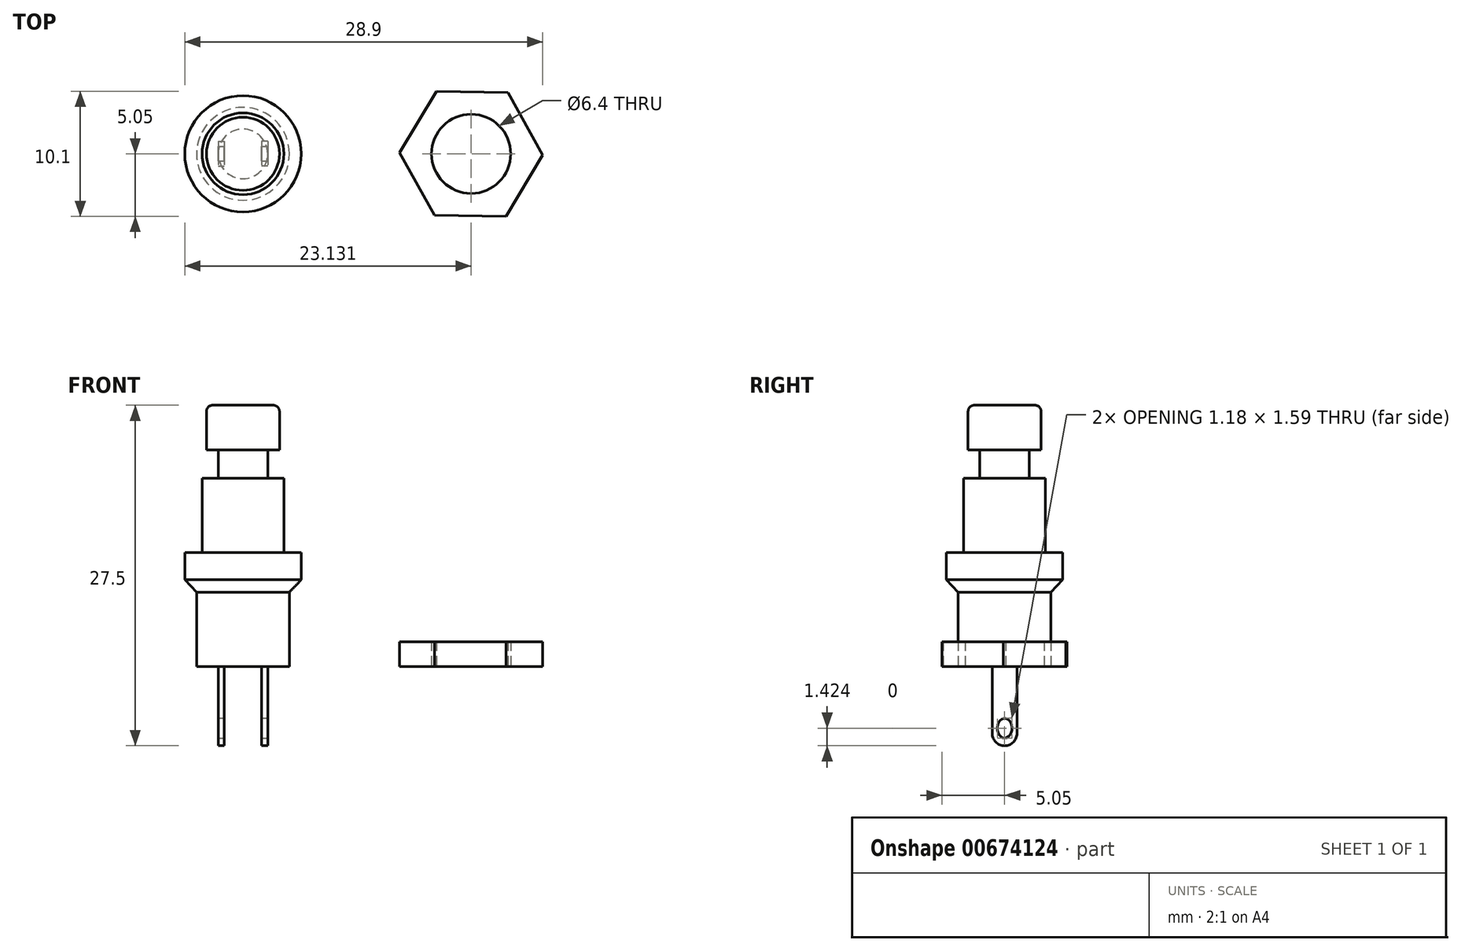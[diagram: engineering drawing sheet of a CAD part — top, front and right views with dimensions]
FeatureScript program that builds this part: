
annotation { "Feature Type Name" : "Feature", "Feature Type Description" : "" }
export const myFeature = defineFeature(function(context is Context, id is Id, definition is map)
    precondition{}
    {
        {
            var Q0;
            Q0=qCreatedBy(makeId("Top.planeOp"),FACE);
            var sketch = newSketch(context, id + "F0", { "sketchPlane" : qUnion([Q0])});
            skCircle(sketch, "E0", {"center": v(0, 0) * mm, "radius": 3.75 * mm});
            skLineSegment(sketch, "E1.bottom", {"start": v(-2, 1) * mm, "end": v(-1.5, 1) * mm});
            skLineSegment(sketch, "E1.top", {"start": v(-2, -1) * mm, "end": v(-1.5, -1) * mm});
            skLineSegment(sketch, "E1.left", {"start": v(-2, 1) * mm, "end": v(-2, -1) * mm});
            skLineSegment(sketch, "E1.right", {"start": v(-1.5, 1) * mm, "end": v(-1.5, -1) * mm});
            skLineSegment(sketch, "E2.MirrorCS", {"start": v(1.5, 1) * mm, "end": v(1.5, -1) * mm});
            skLineSegment(sketch, "E3.MirrorCS", {"start": v(2, 1) * mm, "end": v(1.5, 1) * mm});
            skLineSegment(sketch, "E4.MirrorCS", {"start": v(2, 1) * mm, "end": v(2, -1) * mm});
            skLineSegment(sketch, "E5.MirrorCS", {"start": v(2, -1) * mm, "end": v(1.5, -1) * mm});
            skCircle(sketch, "E6", {"center": v(18.43, 0) * mm, "radius": 3.2 * mm});
            skCircle(sketch, "E7.cCircle", {"center": v(18.43, 0) * mm, "radius": 5 * mm, "construction": true});
            skLineSegment(sketch, "E7.0", {"start": v(21.4, 4.95) * mm, "end": v(24.2, -0.1) * mm});
            skLineSegment(sketch, "E7.1", {"start": v(24.2, -0.1) * mm, "end": v(21.24, -5.05) * mm});
            skLineSegment(sketch, "E7.2", {"start": v(21.24, -5.05) * mm, "end": v(15.46, -4.95) * mm});
            skLineSegment(sketch, "E7.3", {"start": v(15.46, -4.95) * mm, "end": v(12.66, 0.1) * mm});
            skLineSegment(sketch, "E7.4", {"start": v(12.66, 0.1) * mm, "end": v(15.63, 5.05) * mm});
            skLineSegment(sketch, "E7.5", {"start": v(15.63, 5.05) * mm, "end": v(21.4, 4.95) * mm});
            skPoint(sketch, "E7.0.midPoint", {"position": v(22.8, 2.43) * mm});
            skSolve(sketch);
        }
        {
            var Q0;
            Q0=makeQuery(id+"F0.imprint","IMPRINT",FACE,{"disambiguationData":[TD([[makeQuery(id+"F0.imprint","IMPRINT",EDGE,{"derivedFrom":sQuery(id+"F0.wireOp",EDGE,"E0")}),1.0]])]});
            var Q1;
            Q1=makeQuery(id+"F0.imprint","IMPRINT",FACE,{"disambiguationData":[TD([[makeQuery(id+"F0.imprint","IMPRINT",EDGE,{"derivedFrom":sQuery(id+"F0.wireOp",EDGE,"E1.bottom")}),-1.0]])]});
            var Q2;
            Q2=makeQuery(id+"F0.imprint","IMPRINT",FACE,{"disambiguationData":[TD([[makeQuery(id+"F0.imprint","IMPRINT",EDGE,{"derivedFrom":sQuery(id+"F0.wireOp",EDGE,"E2.MirrorCS")}),1.0]])]});
            extrude(context, id + "F1", {"entities" : qUnion([Q0, Q1, Q2]), "depth" : 6 * mm, "offsetDistance" : 25 * mm});
        }
        {
            var Q0;
            Q0=makeQuery(id+"F1.opExtrude","CAP_FACE",FACE,{"disambiguationData":[OSD([sQuery(id+"F0.wireOp",EDGE,"E0")])],"isStart":false});
            cPlane(context, id + "F2", {"entities" : qUnion([Q0]), "cplaneType" : CPlaneType.OFFSET, "offset" : 1 * mm, "width" : 150 * mm, "height" : 150 * mm});
        }
        {
            var Q0;
            Q0=qCreatedBy(id+"F2.planeOp",FACE);
            var sketch = newSketch(context, id + "F3", { "sketchPlane" : qUnion([Q0])});
            skCircle(sketch, "E8", {"center": v(0, 0) * mm, "radius": 4.7 * mm});
            skSolve(sketch);
        }
        {
            var Q1;
            Q1=makeQuery(id+"F3.imprint","IMPRINT",FACE,{"disambiguationData":[TD([[makeQuery(id+"F3.imprint","IMPRINT",EDGE,{"derivedFrom":sQuery(id+"F3.wireOp",EDGE,"E8")}),1.0]])]});
            var Q2;
            Q2=makeQuery(id+"F1.opExtrude","CAP_FACE",FACE,{"disambiguationData":[OSD([sQuery(id+"F0.wireOp",EDGE,"E0")])],"isStart":false});
            loft(context, id + "F4", {"operationType" : NewBodyOperationType.ADD, "sheetProfilesArray" : [{ "sheetProfileEntities" : qUnion([Q1]) }, { "sheetProfileEntities" : qUnion([Q2]) }]});
        }
        {
            var Q0;
            Q0 = qSketchRegion(id + "F3", true);
            extrude(context, id + "F5", {"entities" : qUnion([Q0]), "operationType" : NewBodyOperationType.ADD, "depth" : 2.2 * mm, "offsetDistance" : 25 * mm});
        }
        {
            var Q0;
            Q0=makeQuery(id+"F5.opExtrude","CAP_FACE",FACE,{"disambiguationData":[OSD([sQuery(id+"F3.wireOp",EDGE,"E8")])],"isStart":false});
            var sketch = newSketch(context, id + "F6", { "sketchPlane" : qUnion([Q0])});
            skCircle(sketch, "E9", {"center": v(0, 0) * mm, "radius": 3.3 * mm});
            skSolve(sketch);
        }
        {
            var Q0;
            Q0=makeQuery(id+"F6.imprint","IMPRINT",FACE,{"disambiguationData":[TD([[makeQuery(id+"F6.imprint","IMPRINT",EDGE,{"derivedFrom":sQuery(id+"F6.wireOp",EDGE,"E9")}),1.0]])]});
            var Q1;
            Q1=sQuery(id+"F6.wireOp",EDGE,"E9");
            extrude(context, id + "F7", {"entities" : qUnion([Q0]), "operationType" : NewBodyOperationType.ADD, "surfaceEntities" : qUnion([Q1]), "depth" : 6 * mm, "offsetDistance" : 25 * mm});
        }
        {
            var Q0;
            Q0=makeQuery(id+"F7.opExtrude","CAP_FACE",FACE,{"disambiguationData":[OSD([sQuery(id+"F6.wireOp",EDGE,"E9")])],"isStart":false});
            var sketch = newSketch(context, id + "F8", { "sketchPlane" : qUnion([Q0])});
            skCircle(sketch, "E10", {"center": v(0, 0) * mm, "radius": 2 * mm});
            skSolve(sketch);
        }
        {
            var Q0;
            Q0=makeQuery(id+"F8.imprint","IMPRINT",FACE,{"disambiguationData":[TD([[makeQuery(id+"F8.imprint","IMPRINT",EDGE,{"derivedFrom":sQuery(id+"F8.wireOp",EDGE,"E10")}),1.0]])]});
            extrude(context, id + "F9", {"entities" : qUnion([Q0]), "operationType" : NewBodyOperationType.ADD, "depth" : 2.3 * mm, "offsetDistance" : 25 * mm});
        }
        {
            var Q0;
            Q0=makeQuery(id+"F9.opExtrude","CAP_FACE",FACE,{"disambiguationData":[OSD([sQuery(id+"F8.wireOp",EDGE,"E10")])],"isStart":false});
            var sketch = newSketch(context, id + "F10", { "sketchPlane" : qUnion([Q0])});
            skCircle(sketch, "E11", {"center": v(0, 0) * mm, "radius": 2.95 * mm});
            skSolve(sketch);
        }
        {
            var Q0;
            Q0 = qSketchRegion(id + "F10", true);
            extrude(context, id + "F11", {"entities" : qUnion([Q0]), "depth" : 3.6 * mm, "offsetDistance" : 25 * mm});
        }
        {
            var Q0;
            Q0=makeQuery(id+"F11.opExtrude","CAP_FACE",FACE,{"disambiguationData":[OSD([sQuery(id+"F10.wireOp",EDGE,"E11")])],"isStart":false});
            fillet(context, id + "F12", {"entities" : qUnion([Q0]), "radius" : 0.5 * mm, "tangentPropagation" : true, "allowEdgeOverflow" : false});
        }
        {
            var Q0;
            Q0=makeQuery(id+"F0.imprint","IMPRINT",FACE,{"disambiguationData":[TD([[makeQuery(id+"F0.imprint","IMPRINT",EDGE,{"derivedFrom":sQuery(id+"F0.wireOp",EDGE,"E1.bottom")}),-1.0]])]});
            var Q1;
            Q1=makeQuery(id+"F0.imprint","IMPRINT",FACE,{"disambiguationData":[TD([[makeQuery(id+"F0.imprint","IMPRINT",EDGE,{"derivedFrom":sQuery(id+"F0.wireOp",EDGE,"E2.MirrorCS")}),1.0]])]});
            extrude(context, id + "F13", {"entities" : qUnion([Q0, Q1]), "operationType" : NewBodyOperationType.ADD, "oppositeDirection" : true, "depth" : 6.4 * mm, "offsetDistance" : 25 * mm});
        }
        {
            var Q0;
            Q0=makeQuery(id+"F13.opExtrude","SWEPT_FACE",FACE,{"disambiguationData":[OSD([sQuery(id+"F0.wireOp",EDGE,"E4.MirrorCS")])]});
            var sketch = newSketch(context, id + "F14", { "sketchPlane" : qUnion([Q0])});
            skEllipse(sketch, "E12", {"center": v(0, -4.98) * mm, "majorRadius": 0.8 * mm, "minorRadius": 0.59 * mm, "majorAxis": v(0, -1)});
            skSolve(sketch);
        }
        {
            var Q0;
            Q0=makeQuery(id+"F14.imprint","IMPRINT",FACE,{"disambiguationData":[TD([[makeQuery(id+"F14.imprint","IMPRINT",EDGE,{"derivedFrom":sQuery(id+"F14.wireOp",EDGE,"E12")}),1.0]])]});
            extrude(context, id + "F15", {"entities" : qUnion([Q0]), "operationType" : NewBodyOperationType.REMOVE, "endBound" : BoundingType.THROUGH_ALL, "oppositeDirection" : true, "depth" : 25 * mm, "offsetDistance" : 25 * mm});
        }
        {
            var Q0;
            Q0=makeQuery(id+"F13.opExtrude","CAP_EDGE",EDGE,{"disambiguationData":[OSD([sQuery(id+"F0.wireOp",EDGE,"E3.MirrorCS")])],"isStart":false});
            var Q1;
            Q1=makeQuery(id+"F13.opExtrude","CAP_EDGE",EDGE,{"disambiguationData":[OSD([sQuery(id+"F0.wireOp",EDGE,"E5.MirrorCS")])],"isStart":false});
            var Q2;
            Q2=makeQuery(id+"F13.opExtrude","CAP_EDGE",EDGE,{"disambiguationData":[OSD([sQuery(id+"F0.wireOp",EDGE,"E1.bottom")])],"isStart":false});
            var Q3;
            Q3=makeQuery(id+"F13.opExtrude","CAP_EDGE",EDGE,{"disambiguationData":[OSD([sQuery(id+"F0.wireOp",EDGE,"E1.top")])],"isStart":false});
            fillet(context, id + "F16", {"entities" : qUnion([Q0, Q1, Q2, Q3]), "radius" : 1 * mm, "tangentPropagation" : true, "allowEdgeOverflow" : false});
        }
        {
            var Q0;
            Q0=makeQuery(id+"F0.imprint","IMPRINT",FACE,{"disambiguationData":[TD([[makeQuery(id+"F0.imprint","IMPRINT",EDGE,{"derivedFrom":sQuery(id+"F0.wireOp",EDGE,"E6")}),-1.0]])]});
            extrude(context, id + "F17", {"entities" : qUnion([Q0]), "depth" : 2 * mm, "offsetDistance" : 25 * mm});
        }
    });
